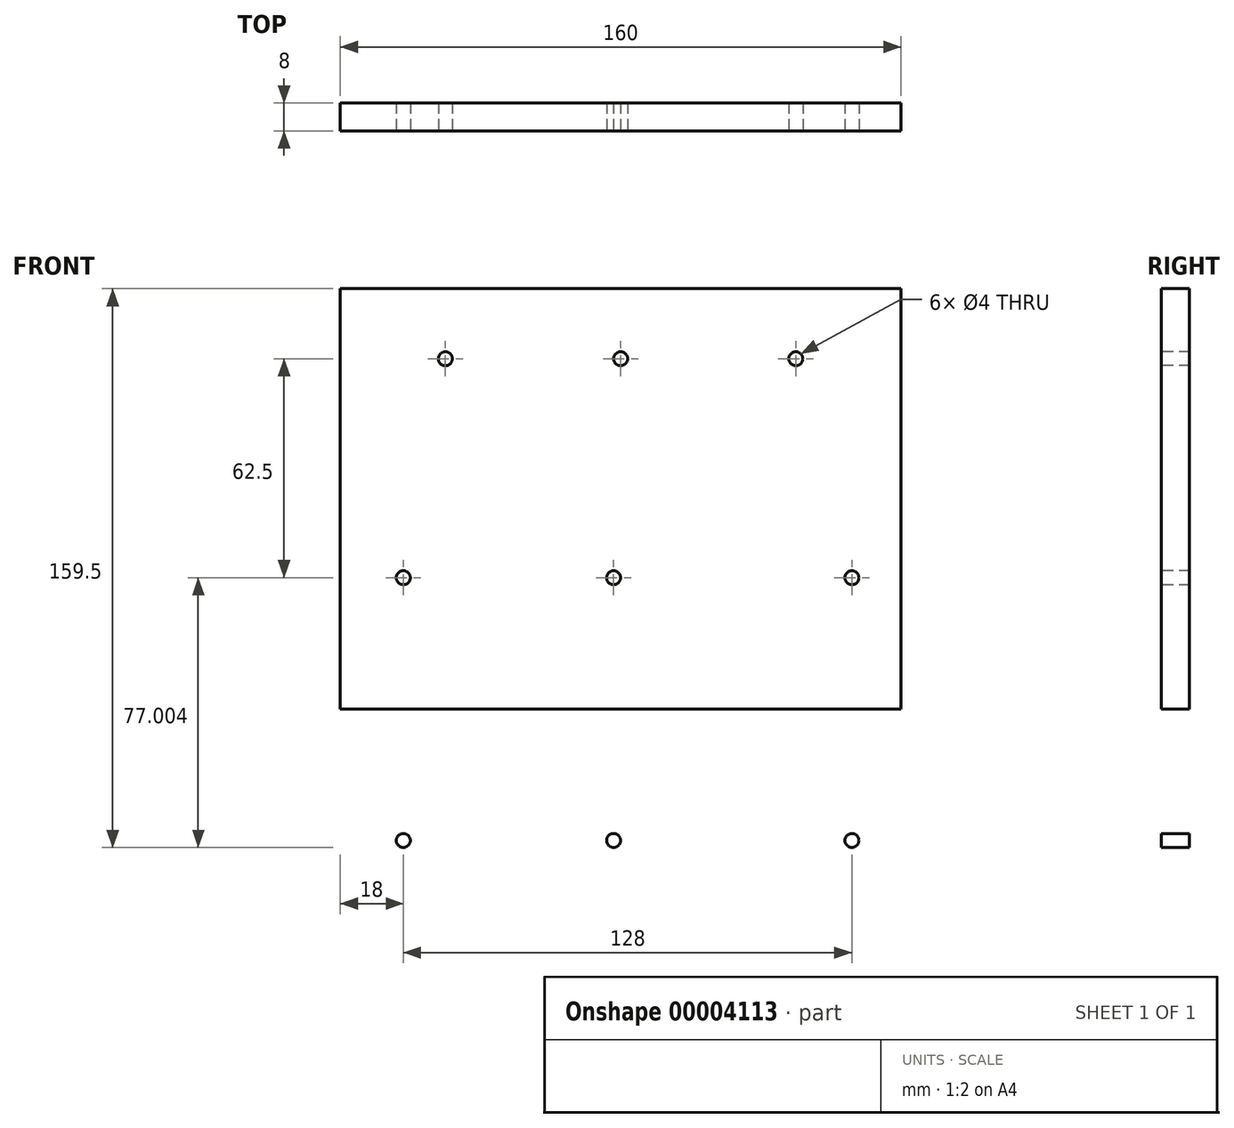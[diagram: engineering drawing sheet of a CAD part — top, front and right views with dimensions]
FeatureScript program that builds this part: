
annotation { "Feature Type Name" : "Feature", "Feature Type Description" : "" }
export const myFeature = defineFeature(function(context is Context, id is Id, definition is map)
    precondition{}
    {
        {
            var Q0;
            Q0=qCreatedBy(makeId("Front.planeOp"),FACE);
            var sketch = newSketch(context, id + "F0", { "sketchPlane" : qUnion([Q0])});
            skLineSegment(sketch, "E0.bottom", {"start": v(0, 55.37) * mm, "end": v(160, 55.37) * mm});
            skLineSegment(sketch, "E0.top", {"start": v(0, -204.63) * mm, "end": v(160, -204.63) * mm});
            skLineSegment(sketch, "E0.left", {"start": v(0, 55.37) * mm, "end": v(0, -204.63) * mm});
            skLineSegment(sketch, "E0.right", {"start": v(160, 55.37) * mm, "end": v(160, -204.63) * mm});
            skSolve(sketch);
        }
        {
            var Q0;
            Q0=makeQuery(id+"F0.imprint","IMPRINT",FACE,{"disambiguationData":[TD([[makeQuery(id+"F0.imprint","IMPRINT",EDGE,{"derivedFrom":sQuery(id+"F0.wireOp",EDGE,"E0.bottom")}),-1.0]])]});
            extrude(context, id + "F1", {"entities" : qUnion([Q0]), "depth" : 8 * mm});
        }
        {
            var Q0;
            Q0=makeQuery(id+"F1.opExtrude","CAP_FACE",FACE,{"disambiguationData":[OSD([sQuery(id+"F0.wireOp",EDGE,"E0.bottom"),sQuery(id+"F0.wireOp",EDGE,"E0.top"),sQuery(id+"F0.wireOp",EDGE,"E0.left"),sQuery(id+"F0.wireOp",EDGE,"E0.right")])],"isStart":false});
            var sketch = newSketch(context, id + "F2", { "sketchPlane" : qUnion([Q0])});
            skCircle(sketch, "E1", {"center": v(146, -27.13) * mm, "radius": 2 * mm});
            skCircle(sketch, "E2", {"center": v(18, -27.13) * mm, "radius": 2 * mm});
            skLineSegment(sketch, "E3", {"start": v(18, -27.13) * mm, "end": v(146, -27.13) * mm});
            skCircle(sketch, "E4", {"center": v(78, -27.13) * mm, "radius": 2 * mm});
            skLineSegment(sketch, "E5", {"start": v(-42.93, -64.63) * mm, "end": v(222.67, -64.63) * mm});
            skCircle(sketch, "E6.0.MirrorC", {"center": v(18, -102.13) * mm, "radius": 2 * mm});
            skCircle(sketch, "E7.0.MirrorC", {"center": v(78, -102.13) * mm, "radius": 2 * mm});
            skCircle(sketch, "E8.0.MirrorC", {"center": v(146, -102.13) * mm, "radius": 2 * mm});
            skSolve(sketch);
        }
        {
            var Q0;
            {var subQ1=sQuery(id+"F2.wireOp",EDGE,"E2");Q0=makeQuery(id+"F2.imprint","IMPRINT",FACE,{"disambiguationData":[TD([[makeQuery(id+"F2.imprint","IMPRINT",EDGE,{"derivedFrom":subQ1}),1.0]])]});}
            var Q1;
            {var subQ1=sQuery(id+"F2.wireOp",EDGE,"E1");Q1=makeQuery(id+"F2.imprint","IMPRINT",FACE,{"disambiguationData":[TD([[makeQuery(id+"F2.imprint","IMPRINT",EDGE,{"derivedFrom":subQ1}),1.0]])]});}
            var Q2;
            {var subQ0=sQuery(id+"F2.wireOp",EDGE,"E4");var subQ1=sQuery(id+"F2.wireOp",EDGE,"E3");var subQ3=makeQuery(id+"F2.imprint","INTERSECT",VERTEX,{"disambiguationData":[OD(0.0)],"derivedFrom":[subQ1,subQ0]});Q2=makeQuery(id+"F2.imprint","IMPRINT",FACE,{"disambiguationData":[TD([[makeQuery(id+"F2.imprint","IMPRINT",EDGE,{"disambiguationData":[TD([[subQ3,-1.0]])],"derivedFrom":subQ1}),1.0]])]});}
            var Q3;
            {var subQ0=sQuery(id+"F2.wireOp",EDGE,"E4");var subQ1=sQuery(id+"F2.wireOp",EDGE,"E3");var subQ3=makeQuery(id+"F2.imprint","INTERSECT",VERTEX,{"disambiguationData":[OD(0.0)],"derivedFrom":[subQ1,subQ0]});Q3=makeQuery(id+"F2.imprint","IMPRINT",FACE,{"disambiguationData":[TD([[makeQuery(id+"F2.imprint","IMPRINT",EDGE,{"disambiguationData":[TD([[subQ3,-1.0]])],"derivedFrom":subQ1}),-1.0]])]});}
            var Q4;
            Q4=makeQuery(id+"F2.imprint","IMPRINT",FACE,{"disambiguationData":[TD([[makeQuery(id+"F2.imprint","IMPRINT",EDGE,{"derivedFrom":sQuery(id+"F2.wireOp",EDGE,"E6.0.MirrorC")}),-1.0]])]});
            var Q5;
            Q5=makeQuery(id+"F2.imprint","IMPRINT",FACE,{"disambiguationData":[TD([[makeQuery(id+"F2.imprint","IMPRINT",EDGE,{"derivedFrom":sQuery(id+"F2.wireOp",EDGE,"E7.0.MirrorC")}),-1.0]])]});
            var Q6;
            Q6=makeQuery(id+"F2.imprint","IMPRINT",FACE,{"disambiguationData":[TD([[makeQuery(id+"F2.imprint","IMPRINT",EDGE,{"derivedFrom":sQuery(id+"F2.wireOp",EDGE,"E8.0.MirrorC")}),-1.0]])]});
            extrude(context, id + "F3", {"entities" : qUnion([Q0, Q1, Q2, Q3, Q4, Q5, Q6]), "operationType" : NewBodyOperationType.REMOVE, "oppositeDirection" : true, "depth" : 25 * mm});
        }
        {
            var Q0;
            Q0=makeQuery(id+"F1.opExtrude","CAP_FACE",FACE,{"disambiguationData":[OSD([sQuery(id+"F0.wireOp",EDGE,"E0.bottom"),sQuery(id+"F0.wireOp",EDGE,"E0.top"),sQuery(id+"F0.wireOp",EDGE,"E0.left"),sQuery(id+"F0.wireOp",EDGE,"E0.right")])],"isStart":false});
            var sketch = newSketch(context, id + "F4", { "sketchPlane" : qUnion([Q0])});
            skLineSegment(sketch, "E9", {"start": v(0, 35.37) * mm, "end": v(160, 35.37) * mm});
            skCircle(sketch, "E10", {"center": v(30, 35.37) * mm, "radius": 2 * mm});
            skCircle(sketch, "E11.1.0.0", {"center": v(80, 35.37) * mm, "radius": 2 * mm});
            skCircle(sketch, "E11.2.0.0", {"center": v(130, 35.37) * mm, "radius": 2 * mm});
            skLineSegment(sketch, "E11.direction1", {"start": v(30, 35.37) * mm, "end": v(80, 35.37) * mm, "construction": true});
            skSolve(sketch);
        }
        {
            var Q0;
            {var subQ0=sQuery(id+"F4.wireOp",EDGE,"E10");var subQ1=sQuery(id+"F4.wireOp",EDGE,"E9");var subQ3=makeQuery(id+"F4.imprint","INTERSECT",VERTEX,{"disambiguationData":[OD(0.0)],"derivedFrom":[subQ1,subQ0]});Q0=makeQuery(id+"F4.imprint","IMPRINT",FACE,{"disambiguationData":[TD([[makeQuery(id+"F4.imprint","IMPRINT",EDGE,{"disambiguationData":[TD([[subQ3,-1.0]])],"derivedFrom":subQ1}),-1.0]])]});}
            var Q1;
            {var subQ0=sQuery(id+"F4.wireOp",EDGE,"E10");var subQ1=sQuery(id+"F4.wireOp",EDGE,"E9");var subQ3=makeQuery(id+"F4.imprint","INTERSECT",VERTEX,{"disambiguationData":[OD(0.0)],"derivedFrom":[subQ1,subQ0]});Q1=makeQuery(id+"F4.imprint","IMPRINT",FACE,{"disambiguationData":[TD([[makeQuery(id+"F4.imprint","IMPRINT",EDGE,{"disambiguationData":[TD([[subQ3,-1.0]])],"derivedFrom":subQ1}),1.0]])]});}
            var Q2;
            {var subQ0=sQuery(id+"F4.wireOp",EDGE,"E11.1.0.0");var subQ1=sQuery(id+"F4.wireOp",EDGE,"E9");var subQ3=makeQuery(id+"F4.imprint","INTERSECT",VERTEX,{"disambiguationData":[OD(0.0)],"derivedFrom":[subQ1,subQ0]});Q2=makeQuery(id+"F4.imprint","IMPRINT",FACE,{"disambiguationData":[TD([[makeQuery(id+"F4.imprint","IMPRINT",EDGE,{"disambiguationData":[TD([[subQ3,-1.0]])],"derivedFrom":subQ1}),-1.0]])]});}
            var Q3;
            {var subQ0=sQuery(id+"F4.wireOp",EDGE,"E11.1.0.0");var subQ1=sQuery(id+"F4.wireOp",EDGE,"E9");var subQ3=makeQuery(id+"F4.imprint","INTERSECT",VERTEX,{"disambiguationData":[OD(0.0)],"derivedFrom":[subQ1,subQ0]});Q3=makeQuery(id+"F4.imprint","IMPRINT",FACE,{"disambiguationData":[TD([[makeQuery(id+"F4.imprint","IMPRINT",EDGE,{"disambiguationData":[TD([[subQ3,-1.0]])],"derivedFrom":subQ1}),1.0]])]});}
            var Q4;
            {var subQ0=sQuery(id+"F4.wireOp",EDGE,"E11.2.0.0");var subQ1=sQuery(id+"F4.wireOp",EDGE,"E9");var subQ3=makeQuery(id+"F4.imprint","INTERSECT",VERTEX,{"disambiguationData":[OD(0.0)],"derivedFrom":[subQ1,subQ0]});Q4=makeQuery(id+"F4.imprint","IMPRINT",FACE,{"disambiguationData":[TD([[makeQuery(id+"F4.imprint","IMPRINT",EDGE,{"disambiguationData":[TD([[subQ3,-1.0]])],"derivedFrom":subQ1}),-1.0]])]});}
            var Q5;
            {var subQ0=sQuery(id+"F4.wireOp",EDGE,"E11.2.0.0");var subQ1=sQuery(id+"F4.wireOp",EDGE,"E9");var subQ3=makeQuery(id+"F4.imprint","INTERSECT",VERTEX,{"disambiguationData":[OD(0.0)],"derivedFrom":[subQ1,subQ0]});Q5=makeQuery(id+"F4.imprint","IMPRINT",FACE,{"disambiguationData":[TD([[makeQuery(id+"F4.imprint","IMPRINT",EDGE,{"disambiguationData":[TD([[subQ3,-1.0]])],"derivedFrom":subQ1}),1.0]])]});}
            extrude(context, id + "F5", {"entities" : qUnion([Q0, Q1, Q2, Q3, Q4, Q5]), "operationType" : NewBodyOperationType.REMOVE, "oppositeDirection" : true, "depth" : 25 * mm});
        }
    });
